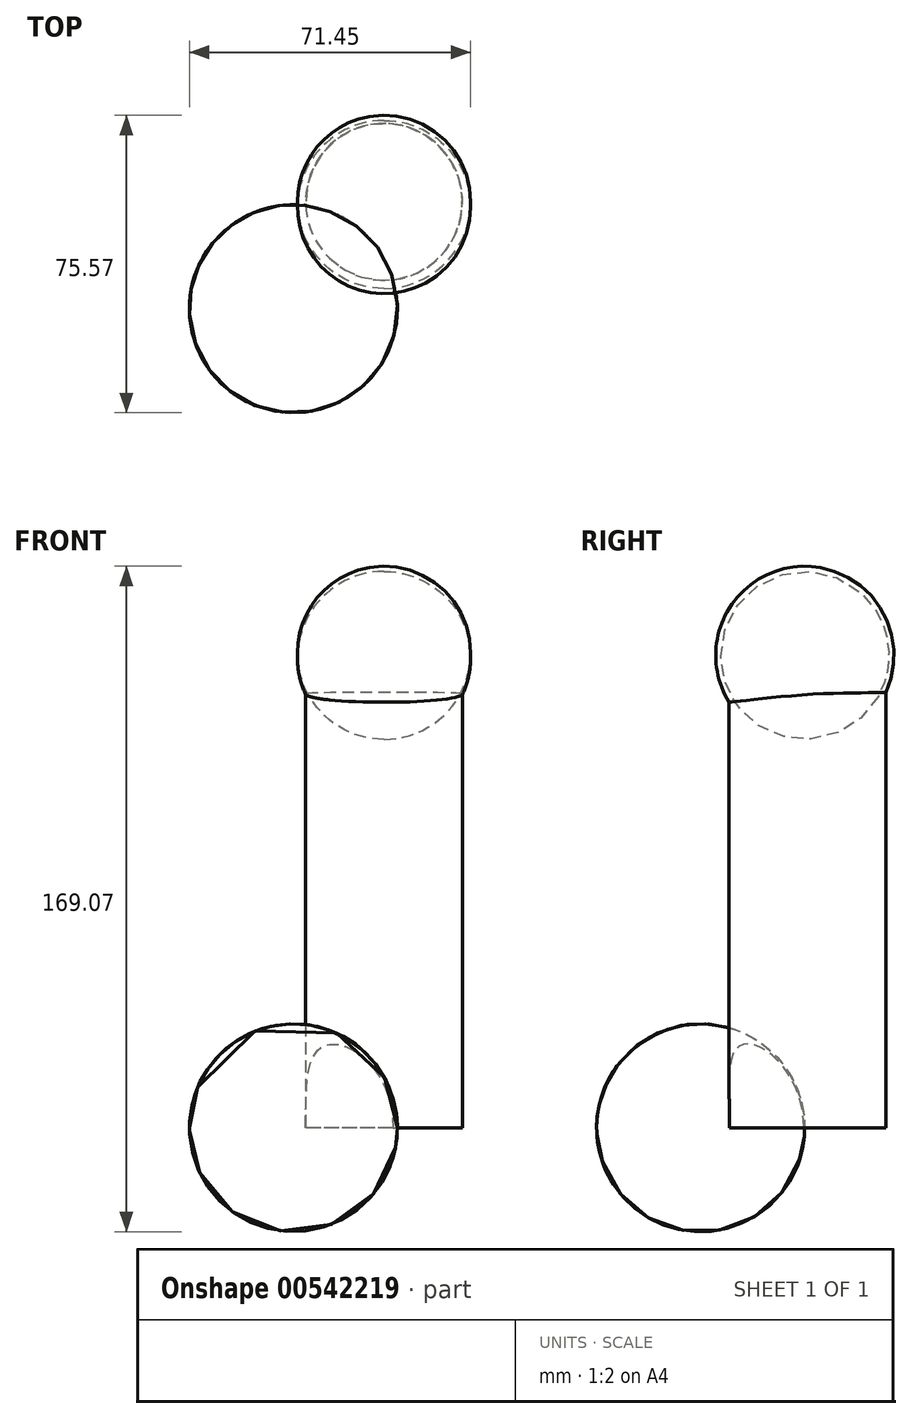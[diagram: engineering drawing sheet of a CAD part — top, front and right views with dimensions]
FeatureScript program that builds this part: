
annotation { "Feature Type Name" : "Feature", "Feature Type Description" : "" }
export const myFeature = defineFeature(function(context is Context, id is Id, definition is map)
    precondition{}
    {
        {
            var Q0;
            Q0=qCreatedBy(makeId("Top.planeOp"),FACE);
            var sketch = newSketch(context, id + "F0", { "sketchPlane" : qUnion([Q0])});
            skArc(sketch, "E0", {"start": v(-10.1, 0) * mm, "mid": v(-36.5, 26.42) * mm, "end": v(-62.93, 0.01) * mm});
            skLineSegment(sketch, "E1", {"start": v(-62.93, 0.01) * mm, "end": v(-10.1, 0) * mm});
            skSolve(sketch);
        }
        {
            var Q0;
            Q0 = qSketchRegion(id + "F0", true);
            var Q1;
            Q1=sQuery(id+"F0.wireOp",EDGE,"E1");
            revolve(context, id + "F1", {"entities" : qUnion([Q0]), "axis" : qUnion([Q1]), "revolveType" : RevolveType.FULL});
        }
        {
            var Q0;
            Q0=qCreatedBy(makeId("Top.planeOp"),FACE);
            var sketch = newSketch(context, id + "F2", { "sketchPlane" : qUnion([Q0])});
            skArc(sketch, "E2", {"start": v(36.51, -0.13) * mm, "mid": v(10.1, 26.3) * mm, "end": v(-16.32, -0.12) * mm});
            skLineSegment(sketch, "E3", {"start": v(-16.32, -0.12) * mm, "end": v(36.51, -0.13) * mm});
            skSolve(sketch);
        }
        {
            var Q0;
            Q0=sQuery(id+"F2.wireOp",EDGE,"E2");
            var Q1;
            Q1=sQuery(id+"F2.wireOp",EDGE,"E3");
            revolve(context, id + "F3", {"bodyType" : ToolBodyType.SURFACE, "surfaceEntities" : qUnion([Q0]), "axis" : qUnion([Q1]), "revolveType" : RevolveType.FULL});
        }
        {
            var Q0;
            Q0=qCreatedBy(makeId("Top.planeOp"),FACE);
            var sketch = newSketch(context, id + "F4", { "sketchPlane" : qUnion([Q0])});
            skCircle(sketch, "E4", {"center": v(-13.48, 27.16) * mm, "radius": 19.93 * mm});
            skSolve(sketch);
        }
        {
            var Q0;
            Q0 = qSketchRegion(id + "F4", true);
            extrude(context, id + "F5", {"entities" : qUnion([Q0]), "operationType" : NewBodyOperationType.ADD, "depth" : 120 * mm, "offsetDistance" : 25 * mm});
        }
        {
            var Q0;
            Q0=makeQuery(id+"F5.opExtrude","CAP_FACE",FACE,{"disambiguationData":[OSD([sQuery(id+"F4.wireOp",EDGE,"E4")])],"isStart":false});
            var sketch = newSketch(context, id + "F6", { "sketchPlane" : qUnion([Q0])});
            skArc(sketch, "E5", {"start": v(8.5, 26.5) * mm, "mid": v(-13.48, 49.15) * mm, "end": v(-35.46, 26.5) * mm});
            skLineSegment(sketch, "E6", {"start": v(-35.46, 26.5) * mm, "end": v(8.5, 26.5) * mm});
            skSolve(sketch);
        }
        {
            var Q0;
            Q0 = qSketchRegion(id + "F6", true);
            var Q1;
            Q1=sQuery(id+"F6.wireOp",EDGE,"E6");
            revolve(context, id + "F7", {"operationType" : NewBodyOperationType.ADD, "entities" : qUnion([Q0]), "axis" : qUnion([Q1]), "revolveType" : RevolveType.FULL});
        }
    });
